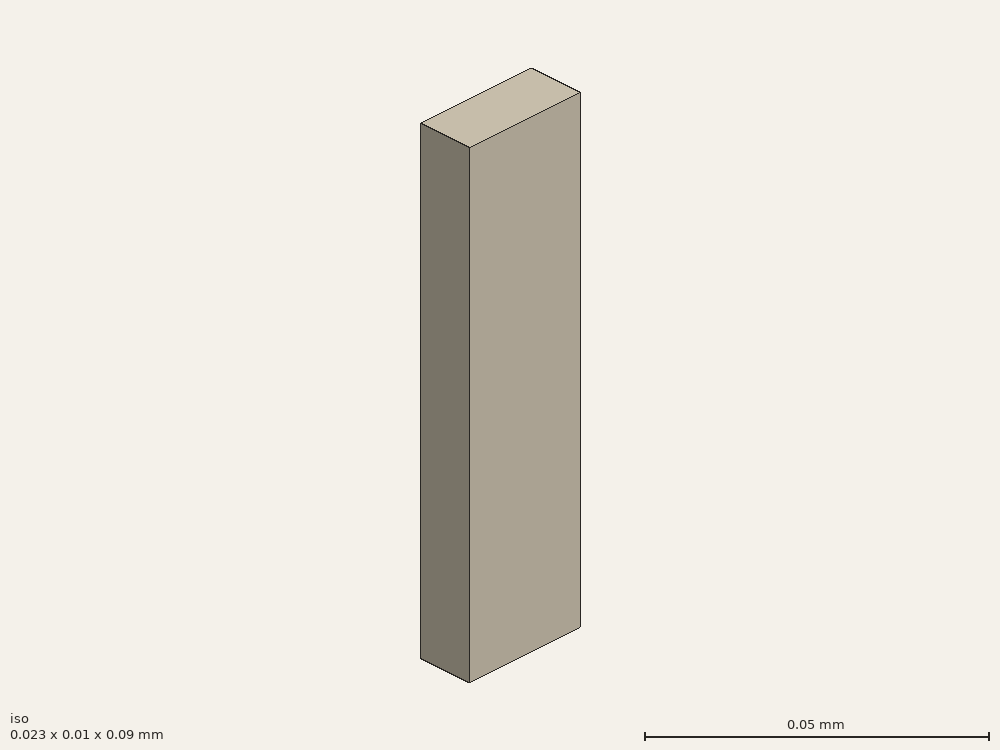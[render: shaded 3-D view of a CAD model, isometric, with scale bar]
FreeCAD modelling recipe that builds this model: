
FCSTD DOCUMENT  (FreeCAD 0.21R33694 (Git))
Label: rectangular_waveguide
License: All rights reserved
LicenseURL: http://en.wikipedia.org/wiki/All_rights_reserved
objects: Part::Part2DObjectPython×4, App::FeaturePython×4, Part::Extrusion×1
note: 5 computed .brp shape members not serialized (recipe doc carries the construction recipe); baked Part::Feature solids carry a one-line shape summary decoded from their .brp

FEATURE [Part::Part2DObjectPython] Rectangle  label="_Pportin"  # Draft 2D object (typed FeaturePython)
  Area = 0.000232258
  ChamferSize = 0
  Columns = 1
  FilletRadius = 0
  Height = 0.01016
  Length = 0.02286
  MakeFace = true
  Placement = pos=(-11.6548,-30.014,0) rot=(0,0,1;0rad)
  Rows = 1
FEATURE [Part::Extrusion] Extrude
  Base = -> Rectangle
  Dir = (0,0,1)
  DirMode = 2
  FaceMakerClass = Part::FaceMakerBullseye
  LengthFwd = 0.09
  LengthRev = 0
  Solid = false
  Symmetric = false
FEATURE [Part::Part2DObjectPython] Rectangle001  label="_Pportout"  # Draft 2D object (typed FeaturePython)
  Area = 0.000232258
  ChamferSize = 0
  Columns = 1
  FilletRadius = 0
  Height = 0.01016
  Length = 0.02286
  MakeFace = true
  Placement = pos=(-11.6548,-30.014,0.09) rot=(0,0,1;0rad)
  Rows = 1
FEATURE [Part::Part2DObjectPython] Line  label="_Pvin"  # Draft 2D object (typed FeaturePython)
  Area = 0
  ChamferSize = 0
  Closed = false
  End = (-11.6434,-30.0039,0)
  FilletRadius = 0
  Length = 0.01016
  MakeFace = true
  Placement = pos=(-11.6434,-30.014,0) rot=(0,0,1;0rad)
  Points = (2) [(0,0,0),(0,0.01016,0)]
  Start = (-11.6434,-30.014,0)
  Subdivisions = 0
FEATURE [Part::Part2DObjectPython] Line001  label="_Pvout"  # Draft 2D object (typed FeaturePython)
  Area = 0
  ChamferSize = 0
  Closed = false
  End = (-11.6434,-30.0039,0.09)
  FilletRadius = 0
  Length = 0.01016
  MakeFace = true
  Placement = pos=(-11.6434,-30.014,0.09) rot=(0,0,1;0rad)
  Points = (2) [(0,0,0),(0,0.01016,0)]
  Start = (-11.6434,-30.014,0.09)
  Subdivisions = 0
FEATURE [App::FeaturePython] Text  label="_Sin(PV){portin}"  # WARN: FeaturePython — macro-defined, semantics opaque (R4)
  Placement = pos=(-11.5437,-30.0762,0.09) rot=(0,0,1;0rad)
  Text = .
FEATURE [App::FeaturePython] Text001  label="_Sout(PV){portout}"  # WARN: FeaturePython — macro-defined, semantics opaque (R4)
  Placement = pos=(-11.5437,-30.0762,0.09) rot=(0,0,1;0rad)
  Text = .
FEATURE [App::FeaturePython] Text002  label="_Min(1,voltage){vin}"  # WARN: FeaturePython — macro-defined, semantics opaque (R4)
  Placement = pos=(-11.5437,-30.0762,0.09) rot=(0,0,1;0rad)
  Text = .
FEATURE [App::FeaturePython] Text003  label="_Mout(2,voltage){vout}"  # WARN: FeaturePython — macro-defined, semantics opaque (R4)
  Placement = pos=(-11.5437,-30.0762,0.09) rot=(0,0,1;0rad)
  Text = .
